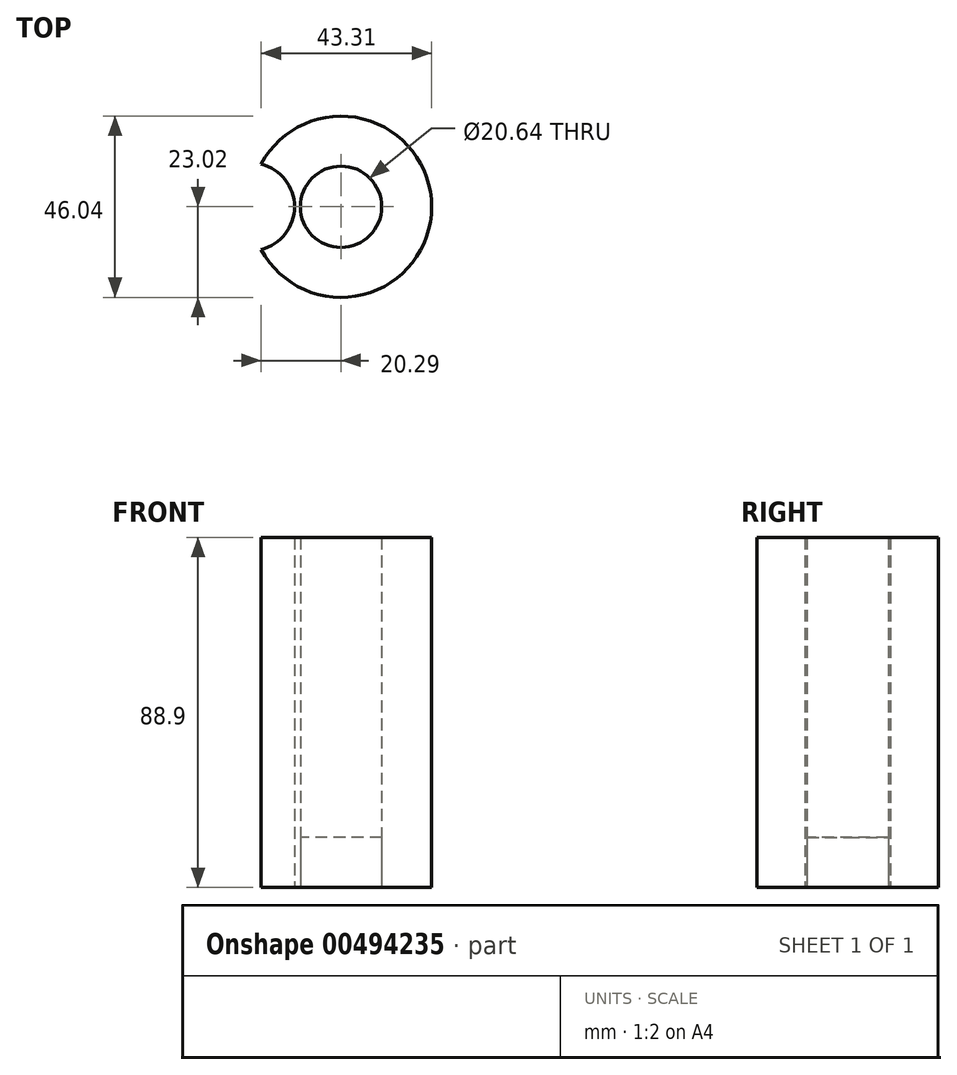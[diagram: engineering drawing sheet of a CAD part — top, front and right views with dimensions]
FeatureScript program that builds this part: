
annotation { "Feature Type Name" : "Feature", "Feature Type Description" : "" }
export const myFeature = defineFeature(function(context is Context, id is Id, definition is map)
    precondition{}
    {
        {
            var Q0;
            Q0=qCreatedBy(makeId("Top.planeOp"),FACE);
            var sketch = newSketch(context, id + "F0", { "sketchPlane" : qUnion([Q0])});
            skCircle(sketch, "E0", {"center": v(0, 0) * mm, "radius": 10.32 * mm});
            skLineSegment(sketch, "E1", {"start": v(-10.32, 0) * mm, "end": v(10.32, 0) * mm, "construction": true});
            skArc(sketch, "E2.0", {"start": v(-20.3, -10.87) * mm, "mid": v(23.02, 0) * mm, "end": v(-20.3, 10.87) * mm});
            skPoint(sketch, "E3", {"position": v(-23.02, 0) * mm});
            skArc(sketch, "E4", {"start": v(-20.3, -10.87) * mm, "mid": v(-11.82, 0) * mm, "end": v(-20.3, 10.87) * mm});
            skLineSegment(sketch, "E5", {"start": v(-20.3, -10.87) * mm, "end": v(-23.02, 0) * mm, "construction": true});
            skSolve(sketch);
        }
        {
            var Q0;
            Q0=makeQuery(id+"F0.imprint","IMPRINT",FACE,{"disambiguationData":[TD([[makeQuery(id+"F0.imprint","IMPRINT",EDGE,{"derivedFrom":sQuery(id+"F0.wireOp",EDGE,"E0")}),1.0]])]});
            extrude(context, id + "F1", {"entities" : qUnion([Q0]), "depth" : 12.7 * mm});
        }
        {
            var Q0;
            Q0=makeQuery(id+"F0.imprint","IMPRINT",FACE,{"disambiguationData":[TD([[makeQuery(id+"F0.imprint","IMPRINT",EDGE,{"derivedFrom":sQuery(id+"F0.wireOp",EDGE,"E0")}),-1.0]])]});
            extrude(context, id + "F2", {"entities" : qUnion([Q0]), "depth" : 88.9 * mm});
        }
    });
